# Revit family: ROYAL PANEL PRO LED4500-940 12X6 HF FP
name_source: partatom
category: Lighting Fixtures
units: mm (PartAtom-declared; Revit-internal decimal feet)

## family parameters
Cut with Voids When Loaded = No
Host = Face
Light Source = Yes
OmniClass Number = 23.80.70.11
OmniClass Title = Luminaries for Internal Lighting
Part Type = Normal
Room Calculation Point = No
Round Connector Dimension = Use Diameter
Shared = No

## types (6) — shared parameters
Assembly Code = D5020200
Body = Thorn_Metal_White
Color Filter = 16777215
Cover = Thorn_PMMA_Opaque
Description = Recessed LED luminaire
Dimming Lamp Color Temperature Shift = <None>
Emit Shape Visible in Rendering = No
Height = 14 mm  [stored 0.0459318 ft]
Lamp = LED
Manufacturer = Thorn Lighting
Tilt Angle = -90.00°
Voltage = 230 V
zero-valued in all types: Default Elevation

## per-type parameters (varying)
| type | Apparent Load | Emit from Rectangle Length | Emit from Rectangle Width | Length | Model | Photometric Web File | URL | Width |
| BETA 2 LED3000 300x1200 | 28 VA | 246 mm  [stored 0.807087 ft] | 1146 mm  [stored 3.75984 ft] | 1196 mm  [stored 3.92388 ft] | 96631473 | TL_BET2_RLO840.IES | www.thornlighting.com/96631473 | 296 mm  [stored 0.971129 ft] |
| BETA 2 LED3800 300x1200 | 36 VA | 246 mm  [stored 0.807087 ft] | 1146 mm  [stored 3.75984 ft] | 1196 mm  [stored 3.92388 ft] | 96631466 | TL_BET2_RHO840.IES | www.thornlighting.com/96631466 | 296 mm  [stored 0.971129 ft] |
| BETA 2 LED3000 M600Q | 25 VA | 546 mm  [stored 1.79134 ft] | 546 mm  [stored 1.79134 ft] | 596 mm  [stored 1.95538 ft] | 96631455 | TL_BET2_QLO840.IES | www.thornlighting.com/96631455 | 596 mm  [stored 1.95538 ft] |
| BETA 2 LED3000 M625Q | 25 VA | 571 mm  [stored 1.87336 ft] | 571 mm  [stored 1.87336 ft] | 621 mm  [stored 2.0374 ft] | 96631459 | TL_BET2_QLO840.IES | www.thornlighting.com/96631459 | 621 mm  [stored 2.0374 ft] |
| BETA 2 LED3800 M600Q | 33 VA | 546 mm  [stored 1.79134 ft] | 546 mm  [stored 1.79134 ft] | 596 mm  [stored 1.95538 ft] | 96631444 | ROYAL PANEL PRO LED4500-940 12X6 HF FP.IES | www.thornlighting.com/96631444 | 596 mm  [stored 1.95538 ft] |
| BETA 2 LED3800 M625Q | 33 VA | 571 mm  [stored 1.87336 ft] | 571 mm  [stored 1.87336 ft] | 621 mm  [stored 2.0374 ft] | 96631448 | TL_BET2_QLO840.IES | www.thornlighting.com/96631448 | 621 mm  [stored 2.0374 ft] |

note: [stored X ft] marks values corroborated as IEEE doubles in the binary element streams (Revit-internal decimal feet)

## geometry (parser evidence)
native form markers: Sweep x2
no freeform markers — native parametric forms only
